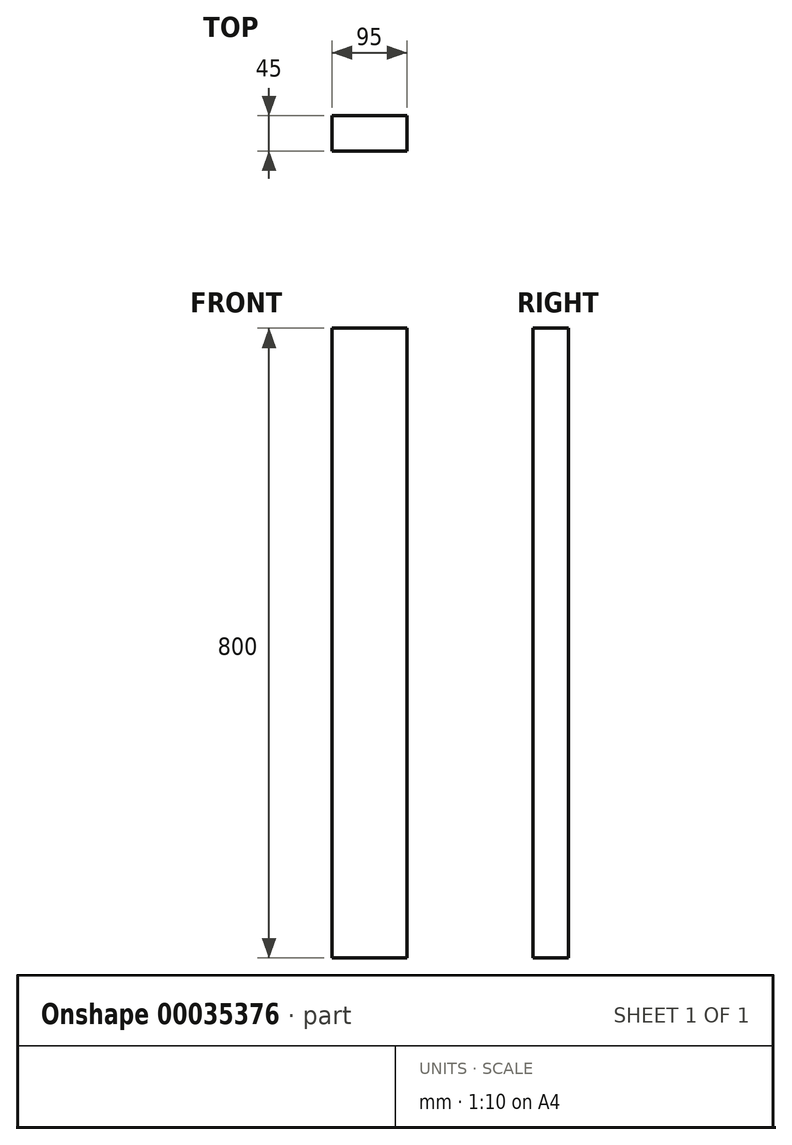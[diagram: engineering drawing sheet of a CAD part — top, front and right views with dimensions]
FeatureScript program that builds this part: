
annotation { "Feature Type Name" : "Feature", "Feature Type Description" : "" }
export const myFeature = defineFeature(function(context is Context, id is Id, definition is map)
    precondition{}
    {
        {
            var Q0;
            Q0=qCreatedBy(makeId("Top.planeOp"),FACE);
            var sketch = newSketch(context, id + "F0", { "sketchPlane" : qUnion([Q0])});
            skLineSegment(sketch, "E0.rect.bottom", {"start": v(47.5, -22.5) * mm, "end": v(-47.5, -22.5) * mm});
            skLineSegment(sketch, "E0.rect.top", {"start": v(47.5, 22.5) * mm, "end": v(-47.5, 22.5) * mm});
            skLineSegment(sketch, "E0.rect.left", {"start": v(47.5, -22.5) * mm, "end": v(47.5, 22.5) * mm});
            skLineSegment(sketch, "E0.rect.right", {"start": v(-47.5, -22.5) * mm, "end": v(-47.5, 22.5) * mm});
            skPoint(sketch, "E0.rect.middle", {"position": v(0, 0) * mm});
            skSolve(sketch);
        }
        {
            var Q0;
            Q0=makeQuery(id+"F0.imprint","IMPRINT",FACE,{"disambiguationData":[TD([[makeQuery(id+"F0.imprint","IMPRINT",EDGE,{"derivedFrom":sQuery(id+"F0.wireOp",EDGE,"E0.rect.bottom")}),-1.0]])]});
            extrude(context, id + "F1", {"entities" : qUnion([Q0]), "depth" : 800 * mm});
        }
    });
